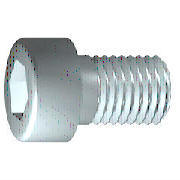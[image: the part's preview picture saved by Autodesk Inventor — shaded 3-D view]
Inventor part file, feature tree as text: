
AUTODESK INVENTOR PART (.ipt)
format: ipt  version: 2022 (Build 260153000, 153)  size: 195,072 bytes
history: native  units: mm (DEFAULTED — no unit token found)
features: sketch x2, extrude x1, plane x1, fillet x1
ambient origin geometry x7: Origin, YZ Plane, XY Plane, X Axis, Y Axis, Z Axis, Center Point
bodies: Solid1 (feature_tree), Body (feature_tree)
feature tree (5):
  extrude  "Slot"  Depth=6.0mm
  plane  "Work Plane1"
  fillet  "Fillet2"  Radius=6.0mm
  sketch  "Sketch1"  dims[d1=13.5mm d2=0.61355mm d3=6.0mm]
  sketch  "Sketch2"  dims[d4=3.0mm d5=60.0deg d6=6.0mm d7=6.0mm d8=5.773503mm d9=10.0mm d10=90.0deg d11=10.0mm d12=0.0mm d13=13.5mm d14=0.0mm d15=0.61345mm d16=0.61345mm d17=0.6mm d19=0.0mm d26=16.0mm d27=45.0deg d28=0.0mm d29=0.0mm d30=0.1mm]
